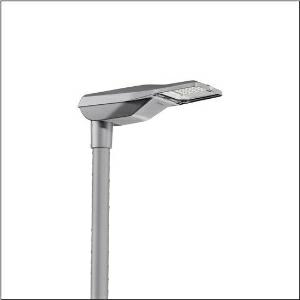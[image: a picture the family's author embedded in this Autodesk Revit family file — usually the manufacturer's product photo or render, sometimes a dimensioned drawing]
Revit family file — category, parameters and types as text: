
# Revit family: streetlight_sl_21_iq_micro___st1_0a_5xe1d31g08cb_12bc
name_source: partatom
category: Lighting Fixtures
units: mm (PartAtom-declared; Revit-internal decimal feet)

## family parameters
Cut with Voids When Loaded = No
Host = Face
Light Source = No
Part Type = Normal
Room Calculation Point = No
Round Connector Dimension = Use Diameter
Shared = No

## types (1)
- --- (1 x LED, 2870 lm, 19.4 W, 3000K)
    Apparent Load = 19 VA
    CIE Flux Codes = 37 72 97 100 100
    Color Rendering = 70
    Color Temperature = 3000K
    Default Elevation = 1800 mm
    Description = Streetlight SL 21 iQ micro, mast luminaire, primary light control with lens, of PMMA, primary optical cover: cover, of toughened safety glass, transparent, light distribution: ST1.0a, light emission: direct distribution, primary light characteristic: asymmetric, installation type: post-top, side-entry, LED, High Power LED, rated luminous flux: 2.870lm, luminous efficacy: 148lm/W, light colour: 730, colour temperature: 3000K, control gear: iQ Street-Remote, control: Street-Remote, Auto-Match, Temp-Guard, Lumen-Switch, Night-Set, Smart-Wire, Light-Fading, Desk-Remote (wireless, voltage-free reading and setting of iQ features in the workshop via application-optimized NFC function/RFID function), optimised constant luminous flux control (CLO 2.0), pre-setting: linear dimming characteristic, mains connection: 220..240V, AC, 50/60Hz, start of lifetime: 19W, end of service life: 20W, reduction: 10W, luminaire housing, of diecast aluminium, powder-coated, Siteco® metallic grey (DB 702S), corrosivity category C5 mid according to DIN EN ISO 12944, please order mast flange separately, inclination adjustable: 0°, 5°, 10°, 15°, sealing non-destructively replaceable, multi-level sealing system, length: 528mm, width: 235mm, height: 110mm, mast flange for spigot size: 42mm (side-entry): 5XC10008XM4, 60/48mm (side-entry/post-top): 5XC10108XM2, 76/60mm (side-entry/post-top): 5XC10108XM1, protection rating (complete): IP66, insulation class (complete): insulation class II (safety insulation), certification: CE, ENEC, ENEC+, VDE, impact resistance: IK10, permissible operating ambient temperature for outdoor applications: -40..+50°C, standard-compliant lighting for roads and squares, packaging unit: 1 piece

Light Distribution: ST1.0a
    Height = 110 mm
    Lamp = 1 x LED
    Lamp Light Flux = 2870 lm
    Lamp Power = 19.4 W
    Lamp count = 1
    Length = 528 mm
    Luminous efficacy = 148 lm/W
    Manufacturer = Siteco
    ModVariant = No
    Model = 5XE1D31G08CB
    Number of Poles = 1
    OnlyDefault = Yes
    Power Factor = 1
    Product Name = Streetlight SL 21 iQ micro | ST1.0a
    Product group = mast luminaire | pylon top
    ProductGroupID = 6100
    Protection Class = Protection class II
    Protection Degree = IP 66
    RLX_Detail_Level = 1
    RLX_Emergency_Light_Flux = 0 lm
    RLX_Emergency_Type = 0
    RLX_Emergency_Type_DB = No
    RlxData = <blob elided: 98813 chars, md5=8f5dc6cf>
    Socket = socket
    Standby Power = 0 W
    System Light Flux = 2870 lm
    System Power = 19 W
    Type Comments = factory setting: luminous flux: 100 % | dim-lin: 254 | 387 mA
    Type Image = l_1006881.jpg
    URL = http://relux.com
    VarID = @adj_139252
    Voltage = 0 V
    Weight = 0.00 kg
    Width = 235 mm

## geometry (parser evidence)
native form markers: Blend x4, Sweep x11
no freeform markers — native parametric forms only
